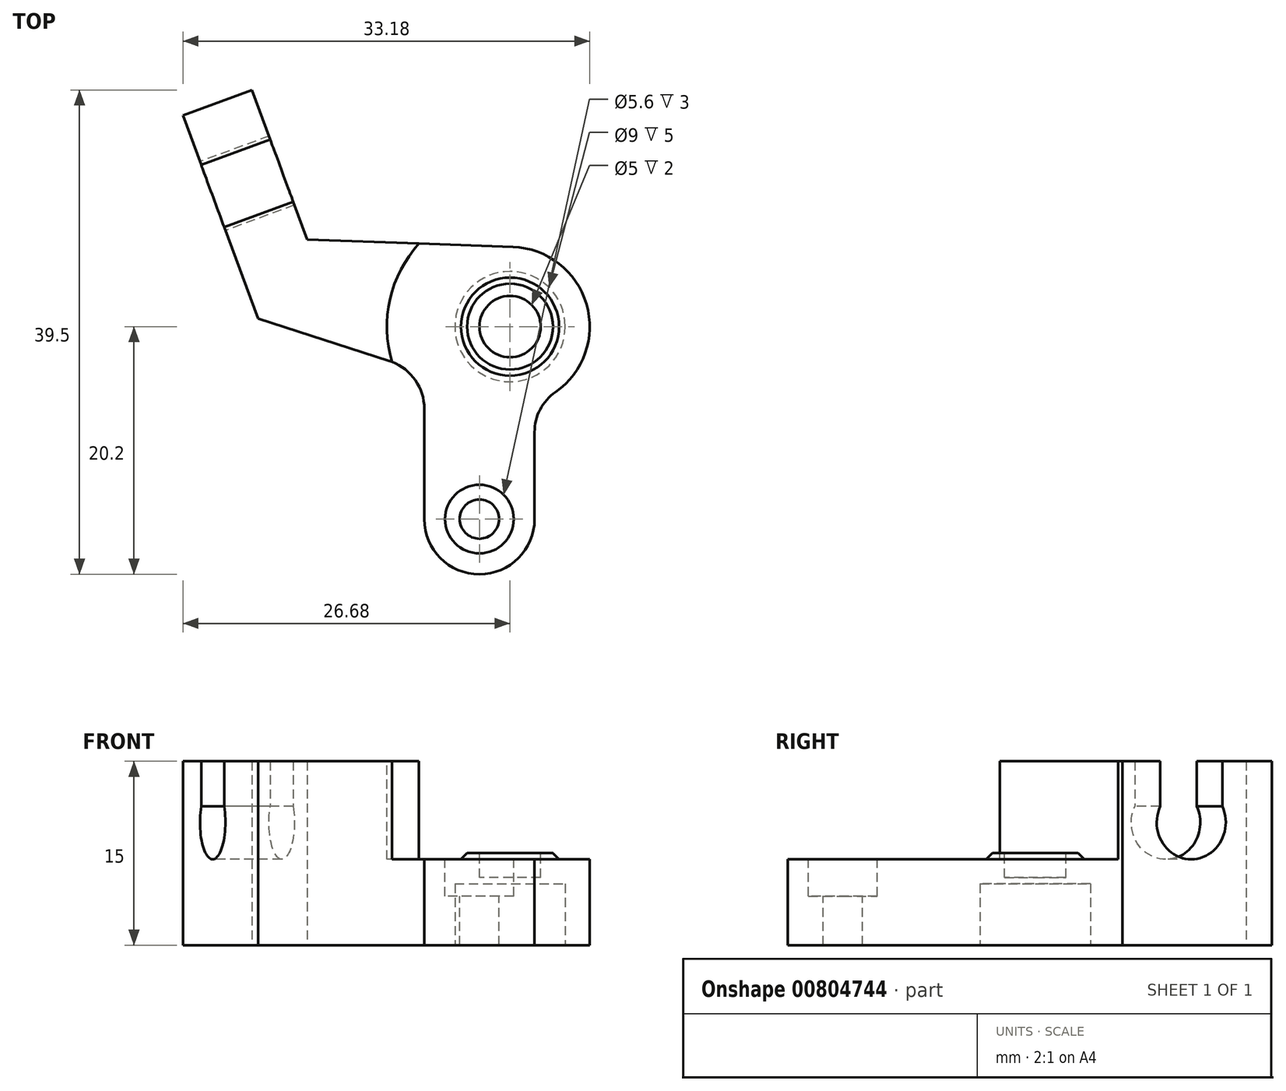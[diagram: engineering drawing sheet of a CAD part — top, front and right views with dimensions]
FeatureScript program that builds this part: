
annotation { "Feature Type Name" : "Feature", "Feature Type Description" : "" }
export const myFeature = defineFeature(function(context is Context, id is Id, definition is map)
    precondition{}
    {
        {
            var Q0;
            Q0=qCreatedBy(makeId("Top.planeOp"),FACE);
            var sketch = newSketch(context, id + "F0", { "sketchPlane" : qUnion([Q0])});
            skArc(sketch, "E0", {"start": v(2, -6.18) * mm, "mid": v(6.44, 0.9) * mm, "end": v(0.23, 6.5) * mm});
            skLineSegment(sketch, "E1", {"start": v(-26.68, 17.22) * mm, "end": v(-21.06, 19.3) * mm});
            skLineSegment(sketch, "E2", {"start": v(-21.06, 19.3) * mm, "end": v(-16.56, 7.1) * mm});
            skLineSegment(sketch, "E3", {"start": v(-16.56, 7.1) * mm, "end": v(0.23, 6.5) * mm});
            skLineSegment(sketch, "E4", {"start": v(2, -6.18) * mm, "end": v(2, -15.7) * mm});
            skArc(sketch, "E5", {"start": v(2, -15.7) * mm, "mid": v(-2.5, -20.2) * mm, "end": v(-7, -15.7) * mm});
            skLineSegment(sketch, "E6", {"start": v(-7, -15.7) * mm, "end": v(-7, -6.7) * mm});
            skLineSegment(sketch, "E7", {"start": v(-20.57, 0.64) * mm, "end": v(-26.68, 17.22) * mm});
            skLineSegment(sketch, "E8", {"start": v(-20.57, 0.64) * mm, "end": v(-9.85, -2.8) * mm});
            skArc(sketch, "E9", {"start": v(-9.85, -2.8) * mm, "mid": v(-7.79, -4.28) * mm, "end": v(-7, -6.7) * mm});
            skSolve(sketch);
        }
        {
            var Q0;
            Q0=qSketchRegion(id+"F0",true);
            extrude(context, id + "F1", {"entities" : qUnion([Q0]), "depth" : 15 * mm, "offsetDistance" : 25 * mm});
        }
        {
            var Q0;
            Q0=makeQuery(id+"F1.opExtrude","CAP_FACE",FACE,{"disambiguationData":[OSD([sQuery(id+"F0.wireOp",EDGE,"E0"),sQuery(id+"F0.wireOp",EDGE,"E1"),sQuery(id+"F0.wireOp",EDGE,"E2"),sQuery(id+"F0.wireOp",EDGE,"E3"),sQuery(id+"F0.wireOp",EDGE,"E4"),sQuery(id+"F0.wireOp",EDGE,"E5"),sQuery(id+"F0.wireOp",EDGE,"E6"),sQuery(id+"F0.wireOp",EDGE,"E7"),sQuery(id+"F0.wireOp",EDGE,"E8"),sQuery(id+"F0.wireOp",EDGE,"E9")])],"isStart":false});
            var sketch = newSketch(context, id + "F2", { "sketchPlane" : qUnion([Q0])});
            skArc(sketch, "E10", {"start": v(2, -9.85) * mm, "mid": v(2.83, 9.64) * mm, "end": v(-7, -7.21) * mm});
            skLineSegment(sketch, "E11.0", {"start": v(-7, -15.7) * mm, "end": v(-7, -7.21) * mm});
            skArc(sketch, "E12.0", {"start": v(2, -15.7) * mm, "mid": v(-2.5, -20.2) * mm, "end": v(-7, -15.7) * mm});
            skLineSegment(sketch, "E13.0", {"start": v(2, -9.85) * mm, "end": v(2, -15.7) * mm});
            skSolve(sketch);
        }
        {
            var Q0;
            Q0=qSketchRegion(id+"F2",true);
            extrude(context, id + "F3", {"entities" : qUnion([Q0]), "operationType" : NewBodyOperationType.REMOVE, "oppositeDirection" : true, "depth" : 8 * mm, "offsetDistance" : 25 * mm});
        }
        {
            var Q0;
            Q0=makeQuery(id+"F3.boolean.opBoolean","COPY",FACE,{"derivedFrom":makeQuery(id+"F3.opExtrude","CAP_FACE",FACE,{"disambiguationData":[OSD([sQuery(id+"F2.wireOp",EDGE,"E10"),sQuery(id+"F2.wireOp",EDGE,"E11.0"),sQuery(id+"F2.wireOp",EDGE,"E12.0"),sQuery(id+"F2.wireOp",EDGE,"E13.0")])],"isStart":false})});
            var sketch = newSketch(context, id + "F4", { "sketchPlane" : qUnion([Q0])});
            skPoint(sketch, "E14", {"position": v(-2.5, -15.7) * mm});
            skSolve(sketch);
        }
        {
            var Q0;
            Q0=sQuery(id+"F4.wireOp",VERTEX,"E14");
            var Q1;
            Q1=makeQuery(id+"F1.opExtrude","SWEPT_BODY",BODY,{"disambiguationData":[OSD([sQuery(id+"F0.wireOp",EDGE,"E0"),sQuery(id+"F0.wireOp",EDGE,"E1"),sQuery(id+"F0.wireOp",EDGE,"E2"),sQuery(id+"F0.wireOp",EDGE,"E3"),sQuery(id+"F0.wireOp",EDGE,"E4"),sQuery(id+"F0.wireOp",EDGE,"E5"),sQuery(id+"F0.wireOp",EDGE,"E6"),sQuery(id+"F0.wireOp",EDGE,"E7"),sQuery(id+"F0.wireOp",EDGE,"E8"),sQuery(id+"F0.wireOp",EDGE,"E9")])]});
            hole(context, id + "F5", {"style" : HoleStyle.C_BORE, "endStyle" : HoleEndStyle.THROUGH, "holeDiameter" : 3.2 * mm, "cBoreDiameter" : 5.6 * mm, "cBoreDepth" : 3 * mm, "isTappedThrough" : true, "tappedDepth" : 12 * mm, "tapClearance" : 3, "locations" : qUnion([Q0]), "scope" : qUnion([Q1])});
        }
        {
            var Q0;
            Q0=makeQuery(id+"F1.opExtrude","CAP_FACE",FACE,{"disambiguationData":[OSD([sQuery(id+"F0.wireOp",EDGE,"E0"),sQuery(id+"F0.wireOp",EDGE,"E1"),sQuery(id+"F0.wireOp",EDGE,"E2"),sQuery(id+"F0.wireOp",EDGE,"E3"),sQuery(id+"F0.wireOp",EDGE,"E4"),sQuery(id+"F0.wireOp",EDGE,"E5"),sQuery(id+"F0.wireOp",EDGE,"E6"),sQuery(id+"F0.wireOp",EDGE,"E7"),sQuery(id+"F0.wireOp",EDGE,"E8"),sQuery(id+"F0.wireOp",EDGE,"E9")])],"isStart":true});
            var sketch = newSketch(context, id + "F6", { "sketchPlane" : qUnion([Q0])});
            skCircle(sketch, "E15", {"center": v(0, 0) * mm, "radius": 4.5 * mm});
            skSolve(sketch);
        }
        {
            var Q0;
            Q0=qSketchRegion(id+"F6",true);
            extrude(context, id + "F7", {"entities" : qUnion([Q0]), "operationType" : NewBodyOperationType.REMOVE, "oppositeDirection" : true, "depth" : 5 * mm, "offsetDistance" : 25 * mm});
        }
        {
            var Q0;
            Q0=makeQuery(id+"F3.boolean.opBoolean","COPY",FACE,{"derivedFrom":makeQuery(id+"F3.opExtrude","CAP_FACE",FACE,{"disambiguationData":[OSD([sQuery(id+"F2.wireOp",EDGE,"E10"),sQuery(id+"F2.wireOp",EDGE,"E11.0"),sQuery(id+"F2.wireOp",EDGE,"E12.0"),sQuery(id+"F2.wireOp",EDGE,"E13.0")])],"isStart":false})});
            var sketch = newSketch(context, id + "F8", { "sketchPlane" : qUnion([Q0])});
            skCircle(sketch, "E16", {"center": v(0, 0) * mm, "radius": 4 * mm});
            skSolve(sketch);
        }
        {
            var Q0;
            Q0=qSketchRegion(id+"F8",true);
            extrude(context, id + "F9", {"entities" : qUnion([Q0]), "operationType" : NewBodyOperationType.ADD, "depth" : 0.5 * mm, "offsetDistance" : 25 * mm});
        }
        {
            var Q0;
            Q0=makeQuery(id+"F9.opExtrude","CAP_FACE",FACE,{"disambiguationData":[OSD([sQuery(id+"F8.wireOp",EDGE,"E16")])],"isStart":false});
            var sketch = newSketch(context, id + "F10", { "sketchPlane" : qUnion([Q0])});
            skCircle(sketch, "E17", {"center": v(0, 0) * mm, "radius": 2.5 * mm});
            skSolve(sketch);
        }
        {
            var Q0;
            Q0=qSketchRegion(id+"F10",true);
            extrude(context, id + "F11", {"entities" : qUnion([Q0]), "operationType" : NewBodyOperationType.REMOVE, "oppositeDirection" : true, "depth" : 2 * mm, "offsetDistance" : 25 * mm});
        }
        {
            var Q0;
            Q0=makeQuery(id+"F9.opExtrude","CAP_EDGE",EDGE,{"disambiguationData":[OSD([sQuery(id+"F8.wireOp",EDGE,"E16")])],"isStart":false});
            chamfer(context, id + "F12", {"entities" : qUnion([Q0]), "width" : 0.5 * mm, "tangentPropagation" : true});
        }
        {
            var Q0;
            Q0=makeQuery(id+"F1.opExtrude","SWEPT_FACE",FACE,{"disambiguationData":[OSD([sQuery(id+"F0.wireOp",EDGE,"E7")])]});
            var sketch = newSketch(context, id + "F13", { "sketchPlane" : qUnion([Q0])});
            skLineSegment(sketch, "E18", {"start": v(-21.1, 15) * mm, "end": v(-21.1, 11.3) * mm});
            skLineSegment(sketch, "E19", {"start": v(-21.1, 15) * mm, "end": v(-15.7, 15) * mm});
            skLineSegment(sketch, "E20", {"start": v(-15.7, 15) * mm, "end": v(-15.7, 11.3) * mm});
            skArc(sketch, "E21", {"start": v(-21.1, 11.3) * mm, "mid": v(-18.4, 7) * mm, "end": v(-15.7, 11.3) * mm});
            skLineSegment(sketch, "E22", {"start": v(-18.4, 10) * mm, "end": v(-18.4, 15) * mm, "construction": true});
            skSolve(sketch);
        }
        {
            var Q0;
            Q0=qSketchRegion(id+"F13",true);
            extrude(context, id + "F14", {"entities" : qUnion([Q0]), "operationType" : NewBodyOperationType.REMOVE, "endBound" : BoundingType.UP_TO_NEXT, "oppositeDirection" : true, "depth" : 25 * mm, "offsetDistance" : 25 * mm});
        }
        {
            var Q0;
            Q0=makeQuery(id+"F1.opExtrude","SWEPT_EDGE",EDGE,{"disambiguationData":[OSD([sQuery(id+"F0.wireOp",EDGE,"E0"),sQuery(id+"F0.wireOp",EDGE,"E4")])]});
            fillet(context, id + "F15", {"entities" : qUnion([Q0]), "radius" : 4 * mm, "tangentPropagation" : true, "allowEdgeOverflow" : false});
        }
    });
